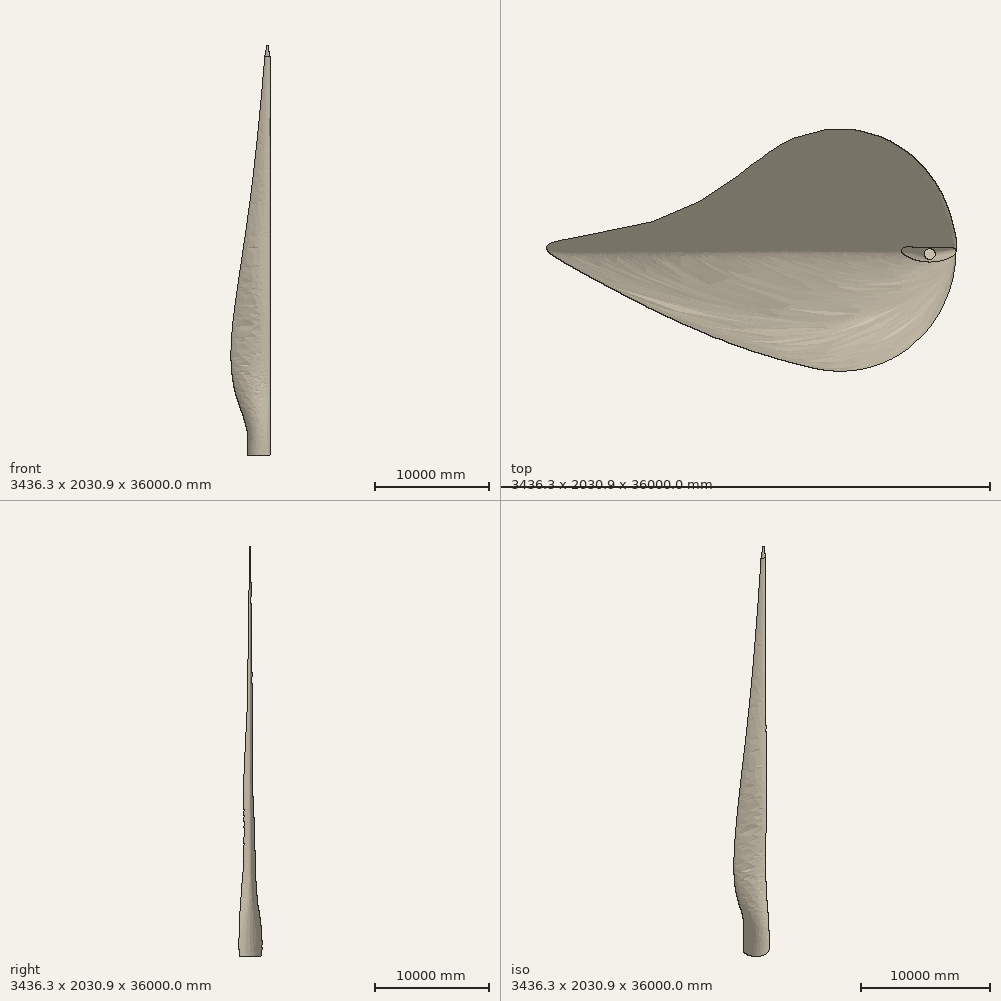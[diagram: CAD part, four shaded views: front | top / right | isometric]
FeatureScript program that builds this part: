
annotation { "Feature Type Name" : "Feature", "Feature Type Description" : "" }
export const myFeature = defineFeature(function(context is Context, id is Id, definition is map)
    precondition{}
    {
        {
            var Q0;
            Q0=qCreatedBy(makeId("Top.planeOp"),FACE);
            var sketch = newSketch(context, id + "F0", { "sketchPlane" : qUnion([Q0])});
            skCircle(sketch, "E0", {"center": v(0, 0) * mm, "radius": 1000 * mm});
            skLineSegment(sketch, "E1.bottom", {"start": v(851.1, 525) * mm, "end": v(-851.1, 525) * mm, "construction": true});
            skLineSegment(sketch, "E1.top", {"start": v(851.1, -525) * mm, "end": v(-851.1, -525) * mm, "construction": true});
            skLineSegment(sketch, "E1.left", {"start": v(851.1, 525) * mm, "end": v(851.1, -525) * mm, "construction": true});
            skLineSegment(sketch, "E1.right", {"start": v(-851.1, 525) * mm, "end": v(-851.1, -525) * mm, "construction": true});
            skLineSegment(sketch, "E2", {"start": v(851.1, 0) * mm, "end": v(0, 0) * mm, "construction": true});
            skSolve(sketch);
        }
        {
            var Q0;
            Q0=qCreatedBy(makeId("Top.planeOp"),FACE);
            cPlane(context, id + "F1", {"entities" : qUnion([Q0]), "cplaneType" : CPlaneType.OFFSET, "offset" : 2000 * mm, "width" : 150 * mm, "height" : 150 * mm});
        }
        {
            var Q0;
            Q0=qCreatedBy(id+"F1.planeOp",FACE);
            var sketch = newSketch(context, id + "F2", { "sketchPlane" : qUnion([Q0])});
            skCircle(sketch, "E3.0", {"center": v(0, 0) * mm, "radius": 1000 * mm});
            skLineSegment(sketch, "E3.1", {"start": v(851.1, 525) * mm, "end": v(-851.1, 525) * mm, "construction": true});
            skLineSegment(sketch, "E3.2", {"start": v(851.1, -525) * mm, "end": v(-851.1, -525) * mm, "construction": true});
            skLineSegment(sketch, "E3.3", {"start": v(851.1, 525) * mm, "end": v(851.1, -525) * mm, "construction": true});
            skLineSegment(sketch, "E3.4", {"start": v(-851.1, 525) * mm, "end": v(-851.1, -525) * mm, "construction": true});
            skLineSegment(sketch, "E3.5", {"start": v(851.1, 0) * mm, "end": v(0, 0) * mm, "construction": true});
            skSolve(sketch);
        }
        {
            var Q0;
            Q0=qCreatedBy(id+"F1.planeOp",FACE);
            cPlane(context, id + "F3", {"entities" : qUnion([Q0]), "cplaneType" : CPlaneType.OFFSET, "offset" : 3000 * mm, "width" : 150 * mm, "height" : 150 * mm});
        }
        {
            var Q0;
            Q0=qCreatedBy(id+"F3.planeOp",FACE);
            var sketch = newSketch(context, id + "F4", { "sketchPlane" : qUnion([Q0])});
            skCircle(sketch, "E4.0", {"center": v(0, 0) * mm, "radius": 1000 * mm, "construction": true});
            skLineSegment(sketch, "E5", {"start": v(1000, 0) * mm, "end": v(-1905.76, 0) * mm, "construction": true});
            skArc(sketch, "E6", {"start": v(-1905.76, 0) * mm, "mid": v(-452.88, -86.82) * mm, "end": v(1000, 0) * mm, "construction": true});
            skCircle(sketch, "E7", {"center": v(-260.37, -85.3) * mm, "radius": 806.72 * mm, "construction": true});
            skFitSpline(sketch, "E8", {"points": [v(-1905.76, 0) * mm, v(-538.74, -842.47) * mm, v(895.67, -232.44) * mm, v(1000, 0) * mm, v(895.78, 292.95) * mm, v(-681.52, 602.75) * mm, v(-1401.57, 263.18) * mm, v(-1905.76, 0) * mm]});
            skSolve(sketch);
        }
        {
            var Q0;
            Q0=qCreatedBy(id+"F3.planeOp",FACE);
            cPlane(context, id + "F5", {"entities" : qUnion([Q0]), "cplaneType" : CPlaneType.OFFSET, "offset" : 5000 * mm, "width" : 150 * mm, "height" : 150 * mm});
        }
        {
            var Q0;
            Q0=qCreatedBy(id+"F5.planeOp",FACE);
            var sketch = newSketch(context, id + "F6", { "sketchPlane" : qUnion([Q0])});
            skLineSegment(sketch, "E9.1", {"start": v(1000, 0) * mm, "end": v(-1905.76, 0) * mm, "construction": true});
            skCircle(sketch, "E9.3", {"center": v(-393.94, -162.13) * mm, "radius": 564.66 * mm, "construction": true});
            skArc(sketch, "E10", {"start": v(-2392.9, 0) * mm, "mid": v(-696.45, -167.4) * mm, "end": v(1000, 0) * mm, "construction": true});
            skLineSegment(sketch, "E11", {"start": v(1000, 0) * mm, "end": v(-2392.9, 0) * mm, "construction": true});
            skFitSpline(sketch, "E12", {"points": [v(-2392.9, 0) * mm, v(0, -566.66) * mm, v(955.1, -116.34) * mm, v(1000, 0) * mm, v(938.88, 167.52) * mm, v(-274.25, 389.69) * mm, v(-1746.7, 78.8) * mm, v(-2392.9, 0) * mm]});
            skSolve(sketch);
        }
        {
            var Q0;
            Q0=qCreatedBy(id+"F5.planeOp",FACE);
            cPlane(context, id + "F7", {"entities" : qUnion([Q0]), "cplaneType" : CPlaneType.OFFSET, "offset" : 5000 * mm, "width" : 150 * mm, "height" : 150 * mm});
        }
        {
            var Q0;
            Q0=qCreatedBy(id+"F7.planeOp",FACE);
            var sketch = newSketch(context, id + "F8", { "sketchPlane" : qUnion([Q0])});
            skLineSegment(sketch, "E13.0", {"start": v(1000, 0) * mm, "end": v(-1905.76, 0) * mm, "construction": true});
            skCircle(sketch, "E13.1", {"center": v(-41.55, -197.63) * mm, "radius": 399.22 * mm, "construction": true});
            skLineSegment(sketch, "E13.3", {"start": v(1000, 0) * mm, "end": v(-2392.9, 0) * mm, "construction": true});
            skFitSpline(sketch, "E13.4", {"points": [v(-2392.9, 0) * mm, v(-2338.2, -131.99) * mm, v(109.83, -949.56) * mm, v(962.16, -156.54) * mm, v(1007.07, -4.51) * mm, v(991.32, 275.8) * mm, v(-412.14, 543.94) * mm, v(-1541.72, -2.41) * mm, v(-2421.05, 67.91) * mm, v(-2392.9, 0) * mm], "construction": true});
            skArc(sketch, "E14", {"start": v(-1816.62, 0) * mm, "mid": v(-408.31, -211.69) * mm, "end": v(1000, 0) * mm, "construction": true});
            skFitSpline(sketch, "E15", {"points": [v(-1816.62, 0) * mm, v(-75.33, -595.41) * mm, v(945.5, -129.55) * mm, v(1000, 0) * mm, v(933.83, 97.72) * mm, v(-75.33, 200.16) * mm, v(-1151.9, 32.5) * mm, v(-1816.62, 0) * mm]});
            skSolve(sketch);
        }
        {
            var Q0;
            Q0=qCreatedBy(id+"F7.planeOp",FACE);
            cPlane(context, id + "F9", {"entities" : qUnion([Q0]), "cplaneType" : CPlaneType.OFFSET, "offset" : 5000 * mm, "width" : 150 * mm, "height" : 150 * mm});
        }
        {
            var Q0;
            Q0=qCreatedBy(id+"F9.planeOp",FACE);
            var sketch = newSketch(context, id + "F10", { "sketchPlane" : qUnion([Q0])});
            skLineSegment(sketch, "E16.0", {"start": v(1000, 0) * mm, "end": v(-1905.76, 0) * mm, "construction": true});
            skCircle(sketch, "E16.1", {"center": v(75.87, -95.47) * mm, "radius": 277.22 * mm, "construction": true});
            skLineSegment(sketch, "E16.2", {"start": v(1000, 0) * mm, "end": v(-2392.9, 0) * mm, "construction": true});
            skArc(sketch, "E17", {"start": v(-1078.3, 0) * mm, "mid": v(-39.15, -96.65) * mm, "end": v(1000, 0) * mm, "construction": true});
            skFitSpline(sketch, "E18", {"points": [v(-1078.3, 0) * mm, v(30.74, -369) * mm, v(915.63, -167.35) * mm, v(1000, 0) * mm, v(872.32, 136.27) * mm, v(30.74, 178.05) * mm, v(-533.72, 47.05) * mm, v(-1078.3, 0) * mm]});
            skSolve(sketch);
        }
        {
            var Q0;
            Q0=qCreatedBy(id+"F9.planeOp",FACE);
            cPlane(context, id + "F11", {"entities" : qUnion([Q0]), "cplaneType" : CPlaneType.OFFSET, "offset" : 15000 * mm, "width" : 150 * mm, "height" : 150 * mm});
        }
        {
            var Q0;
            Q0=qCreatedBy(id+"F11.planeOp",FACE);
            var sketch = newSketch(context, id + "F12", { "sketchPlane" : qUnion([Q0])});
            skLineSegment(sketch, "E19.0", {"start": v(1000, 0) * mm, "end": v(-1905.76, 0) * mm, "construction": true});
            skLineSegment(sketch, "E19.2", {"start": v(1000, 0) * mm, "end": v(-2392.9, 0) * mm, "construction": true});
            skCircle(sketch, "E20", {"center": v(780.88, -29.93) * mm, "radius": 74.07 * mm, "construction": true});
            skArc(sketch, "E21", {"start": v(540.83, 0) * mm, "mid": v(770.42, -29.99) * mm, "end": v(1000, 0) * mm, "construction": true});
            skFitSpline(sketch, "E22", {"points": [v(540.83, 0) * mm, v(738.5, -90.67) * mm, v(985.23, -35.23) * mm, v(1000, 0) * mm, v(979.68, 25.85) * mm, v(734.03, 27.44) * mm, v(574.3, 31.4) * mm, v(540.83, 0) * mm]});
            skSolve(sketch);
        }
        {
            var Q0;
            Q0=qCreatedBy(id+"F11.planeOp",FACE);
            cPlane(context, id + "F13", {"entities" : qUnion([Q0]), "cplaneType" : CPlaneType.OFFSET, "offset" : 1000 * mm, "oppositeDirection" : true, "width" : 150 * mm, "height" : 150 * mm});
        }
        {
            var Q0;
            Q0=qCreatedBy(id+"F9.planeOp",FACE);
            cPlane(context, id + "F14", {"entities" : qUnion([Q0]), "cplaneType" : CPlaneType.OFFSET, "offset" : 5000 * mm, "width" : 150 * mm, "height" : 150 * mm});
        }
        {
            var Q0;
            Q0=qCreatedBy(id+"F14.planeOp",FACE);
            var sketch = newSketch(context, id + "F15", { "sketchPlane" : qUnion([Q0])});
            skLineSegment(sketch, "E23.0", {"start": v(1000, 0) * mm, "end": v(-1905.76, 0) * mm, "construction": true});
            skCircle(sketch, "E23.1", {"center": v(462.37, -47.75) * mm, "radius": 187.93 * mm, "construction": true});
            skArc(sketch, "E24", {"start": v(-426.95, 0) * mm, "mid": v(286.52, -50.82) * mm, "end": v(1000, 0) * mm, "construction": true});
            skFitSpline(sketch, "E25", {"points": [v(-426.95, 0) * mm, v(444.7, -234.84) * mm, v(977.35, -48.24) * mm, v(1000, 0) * mm, v(966.35, 61.82) * mm, v(464.87, 140.17) * mm, v(-44.05, 48.62) * mm, v(-426.95, 0) * mm]});
            skSolve(sketch);
        }
        {
            var Q0;
            Q0=qCreatedBy(id+"F11.planeOp",FACE);
            cPlane(context, id + "F16", {"entities" : qUnion([Q0]), "cplaneType" : CPlaneType.OFFSET, "offset" : 1000 * mm, "width" : 150 * mm, "height" : 150 * mm});
        }
        {
            var Q0;
            Q0=qCreatedBy(id+"F16.planeOp",FACE);
            var sketch = newSketch(context, id + "F17", { "sketchPlane" : qUnion([Q0])});
            skCircle(sketch, "E26", {"center": v(781.13, -27.33) * mm, "radius": 46.13 * mm});
            skSolve(sketch);
        }
        {
            var Q0;
            Q0=qCreatedBy(id+"F16.planeOp",FACE);
            cPlane(context, id + "F18", {"entities" : qUnion([Q0]), "cplaneType" : CPlaneType.OFFSET, "offset" : 1000 * mm, "width" : 150 * mm, "height" : 150 * mm});
        }
        {
            var Q0;
            Q0=makeQuery(id+"F0.imprint","IMPRINT",FACE,{"disambiguationData":[TD([[makeQuery(id+"F0.imprint","IMPRINT",EDGE,{"derivedFrom":sQuery(id+"F0.wireOp",EDGE,"E0")}),1.0]])]});
            var Q1;
            Q1=makeQuery(id+"F2.imprint","IMPRINT",FACE,{"disambiguationData":[TD([[makeQuery(id+"F2.imprint","IMPRINT",EDGE,{"derivedFrom":sQuery(id+"F2.wireOp",EDGE,"E3.0")}),1.0]])]});
            var Q2;
            Q2=makeQuery(id+"F4.imprint","IMPRINT",FACE,{"disambiguationData":[TD([[makeQuery(id+"F4.imprint","IMPRINT",EDGE,{"derivedFrom":sQuery(id+"F4.wireOp",EDGE,"E8")}),1.0]])]});
            var Q3;
            Q3=makeQuery(id+"F6.imprint","IMPRINT",FACE,{"disambiguationData":[TD([[makeQuery(id+"F6.imprint","IMPRINT",EDGE,{"derivedFrom":sQuery(id+"F6.wireOp",EDGE,"E12")}),1.0]])]});
            var Q4;
            Q4=makeQuery(id+"F8.imprint","IMPRINT",FACE,{"disambiguationData":[TD([[makeQuery(id+"F8.imprint","IMPRINT",EDGE,{"derivedFrom":sQuery(id+"F8.wireOp",EDGE,"E15")}),1.0]])]});
            var Q5;
            Q5=makeQuery(id+"F10.imprint","IMPRINT",FACE,{"disambiguationData":[TD([[makeQuery(id+"F10.imprint","IMPRINT",EDGE,{"derivedFrom":sQuery(id+"F10.wireOp",EDGE,"E18")}),1.0]])]});
            var Q6;
            Q6=makeQuery(id+"F15.imprint","IMPRINT",FACE,{"disambiguationData":[TD([[makeQuery(id+"F15.imprint","IMPRINT",EDGE,{"derivedFrom":sQuery(id+"F15.wireOp",EDGE,"E25")}),1.0]])]});
            var Q7;
            Q7=makeQuery(id+"F12.imprint","IMPRINT",FACE,{"disambiguationData":[TD([[makeQuery(id+"F12.imprint","IMPRINT",EDGE,{"derivedFrom":sQuery(id+"F12.wireOp",EDGE,"E22")}),1.0]])]});
            loft(context, id + "F19", {"sheetProfilesArray" : [{ "sheetProfileEntities" : qUnion([Q0]) }, { "sheetProfileEntities" : qUnion([Q1]) }, { "sheetProfileEntities" : qUnion([Q2]) }, { "sheetProfileEntities" : qUnion([Q3]) }, { "sheetProfileEntities" : qUnion([Q4]) }, { "sheetProfileEntities" : qUnion([Q5]) }, { "sheetProfileEntities" : qUnion([Q6]) }, { "sheetProfileEntities" : qUnion([Q7]) }]});
        }
        {
            var Q0;
            Q0=makeQuery(id+"F12.imprint","IMPRINT",FACE,{"disambiguationData":[TD([[makeQuery(id+"F12.imprint","IMPRINT",EDGE,{"derivedFrom":sQuery(id+"F12.wireOp",EDGE,"E22")}),1.0]])]});
            var Q1;
            Q1=makeQuery(id+"F17.imprint","IMPRINT",FACE,{"disambiguationData":[TD([[makeQuery(id+"F17.imprint","IMPRINT",EDGE,{"derivedFrom":sQuery(id+"F17.wireOp",EDGE,"E26")}),1.0]])]});
            loft(context, id + "F20", {"operationType" : NewBodyOperationType.ADD, "sheetProfilesArray" : [{ "sheetProfileEntities" : qUnion([Q0]) }, { "sheetProfileEntities" : qUnion([Q1]) }]});
        }
    });
